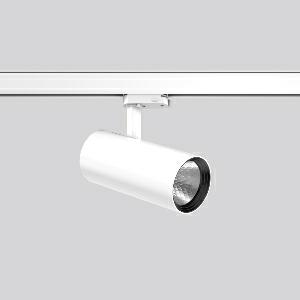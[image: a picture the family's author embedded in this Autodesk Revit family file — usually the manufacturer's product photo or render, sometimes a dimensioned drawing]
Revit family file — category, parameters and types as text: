
# Revit family: deecos_s_mini_742195_002_2_76_4db8
name_source: partatom
category: Lighting Fixtures
units: mm (PartAtom-declared; Revit-internal decimal feet)

## family parameters
Cut with Voids When Loaded = No
Host = Face
Light Source = No
Part Type = Normal
Room Calculation Point = No
Round Connector Dimension = Use Diameter
Shared = No

## types (1)
- DEECOS S mini (1 x LED Modul 927, 2400 lm, 2700)
    Apparent Load = 20 VA
    Approval mark = CE
    CIE Flux Codes = 100 100 100 100 100
    Color Rendering = 92
    Color Temperature = 2700
    Default Elevation = 1800 mm
    Description = Series: DEECOS S mini
LED surface-mounted projector in modern design with no visible cooling ribs. Housing: die-cast aluminium, powder-coated. Rotation range: 356°. Swivel range: 90°. Black plastic ring and recessed LED to prevent glare from the side. Optical assembly with reflector made of MIRO-Silver with 98% total light reflection for outstanding efficiency - can be changed without tools. Best colour rendering index Ra>90. With adapter for RZB 3-circuit DALI tracks. Suitable for Track on ceiling, Wall track. High quality converter without flickering and stroboscopic effect. The following accessories can be mounted without use of tools: interchangeable lenses, decorative glasses, honeycomb louvre, clear and frosted diffusers, white interchangeable plastic ring. 
Colour: traffic white, matt (RAL 9016)
Diameter: 87 mm
Height: 214 mm
Lamp: LED
Socket: without socket
Colour temperature: 2700K
Colour rendering index (CRI): 92
System power: 20 W
Rated luminous flux: 2400 lm
Luminous efficiency: 120 lm/W
Control gear: Converter, dimmable, DALI
Protection class: I
Type of protection: IP 20
    Height = 214 mm
    Lamp = 1 x LED Modul 927
    Lamp Light Flux = 2400 lm
    Lamp count = 1
    Length = 87 mm
    Lifetime = 50000 h
    Luminous efficacy = 120 lm/W
    Manufacturer = RZB
    ModVariant = No
    Model = 742195.002.2.76
    Mounting Place = Ceiling
    Mounting Type = Rail mounted
    Number of Poles = 1
    OnlyDefault = Yes
    Power Factor = 1
    Product Name = DEECOS S mini
    Product group = Track mounted projectors
    ProductGroupID = 301
    Protection Class = Protection class I
    Protection Degree = IP 20
    RLX_Detail_Level = 1
    RLX_Emergency_Light_Flux = 0 lm
    RLX_Emergency_Type = 0
    RLX_Emergency_Type_DB = No
    RlxData = <blob elided: 35445 chars, md5=5875f73c>
    Socket = socket
    Standby Power = 0 W
    System Light Flux = 2400 lm
    System Power = 20 W
    Type Comments = Product without accessories
    Type Image = 741926.002.jpg
    URL = http://relux.com
    VarID = ---
    Voltage = 230 V
    Voltage Range = 220-240 V
    Weight = 0.00 kg
    Width = 0 mm  [stored 0 ft]

note: [stored X ft] marks values corroborated as IEEE doubles in the binary element streams (Revit-internal decimal feet)

## geometry (parser evidence)
native form markers: Blend x4, Sweep x11
no freeform markers — native parametric forms only
